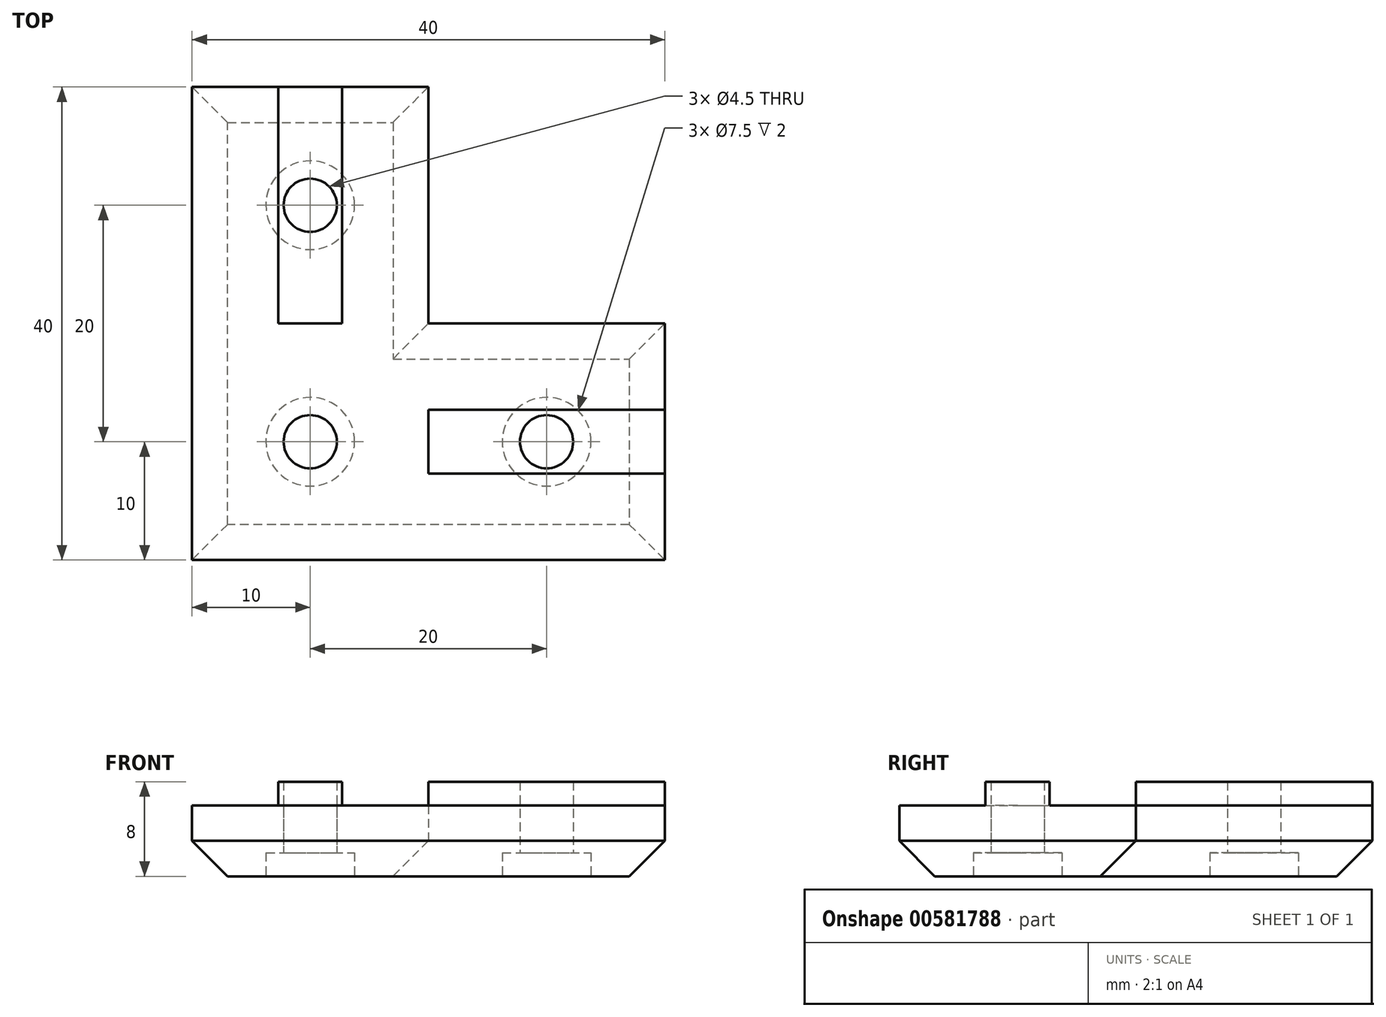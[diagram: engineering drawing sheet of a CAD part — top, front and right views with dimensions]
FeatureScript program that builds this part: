
annotation { "Feature Type Name" : "Feature", "Feature Type Description" : "" }
export const myFeature = defineFeature(function(context is Context, id is Id, definition is map)
    precondition{}
    {
        {
            var Q0;
            Q0=qCreatedBy(makeId("Top.planeOp"),FACE);
            var sketch = newSketch(context, id + "F0", { "sketchPlane" : qUnion([Q0])});
            skLineSegment(sketch, "E0", {"start": v(0, 0) * mm, "end": v(0, 40) * mm});
            skLineSegment(sketch, "E1", {"start": v(0, 40) * mm, "end": v(20, 40) * mm});
            skLineSegment(sketch, "E2", {"start": v(20, 40) * mm, "end": v(20, 20) * mm});
            skLineSegment(sketch, "E3", {"start": v(20, 20) * mm, "end": v(40, 20) * mm});
            skLineSegment(sketch, "E4", {"start": v(40, 20) * mm, "end": v(40, 0) * mm});
            skLineSegment(sketch, "E5", {"start": v(40, 0) * mm, "end": v(0, 0) * mm});
            skSolve(sketch);
        }
        {
            var Q0;
            Q0=qSketchRegion(id+"F0",true);
            extrude(context, id + "F1", {"entities" : qUnion([Q0]), "depth" : 6 * mm});
        }
        {
            var Q0;
            Q0=makeQuery(id+"F1.opExtrude","CAP_FACE",FACE,{"disambiguationData":[OSD([sQuery(id+"F0.wireOp",EDGE,"E0"),sQuery(id+"F0.wireOp",EDGE,"E1"),sQuery(id+"F0.wireOp",EDGE,"E2"),sQuery(id+"F0.wireOp",EDGE,"E3"),sQuery(id+"F0.wireOp",EDGE,"E4"),sQuery(id+"F0.wireOp",EDGE,"E5")])],"isStart":false});
            var sketch = newSketch(context, id + "F2", { "sketchPlane" : qUnion([Q0])});
            skLineSegment(sketch, "E6", {"start": v(7.3, 40) * mm, "end": v(12.71, 40) * mm});
            skLineSegment(sketch, "E7", {"start": v(12.71, 40) * mm, "end": v(12.71, 20) * mm});
            skLineSegment(sketch, "E8", {"start": v(12.71, 20) * mm, "end": v(10, 20) * mm});
            skPoint(sketch, "E8.endSnap0", {"position": v(10, 40) * mm});
            skLineSegment(sketch, "E9", {"start": v(10, 20) * mm, "end": v(7.3, 20) * mm});
            skLineSegment(sketch, "E10", {"start": v(7.3, 20) * mm, "end": v(7.3, 40) * mm});
            skLineSegment(sketch, "E11", {"start": v(40, 12.71) * mm, "end": v(40, 7.3) * mm});
            skLineSegment(sketch, "E12", {"start": v(40, 7.3) * mm, "end": v(20, 7.3) * mm});
            skLineSegment(sketch, "E13", {"start": v(20, 7.3) * mm, "end": v(20, 10) * mm});
            skPoint(sketch, "E13.endSnap0", {"position": v(40, 10) * mm});
            skLineSegment(sketch, "E14", {"start": v(20, 10) * mm, "end": v(20, 12.71) * mm});
            skLineSegment(sketch, "E15", {"start": v(20, 12.71) * mm, "end": v(40, 12.71) * mm});
            skSolve(sketch);
        }
        {
            var Q0;
            Q0=qSketchRegion(id+"F2",true);
            extrude(context, id + "F3", {"entities" : qUnion([Q0]), "operationType" : NewBodyOperationType.ADD, "depth" : 2 * mm});
        }
        {
            var Q0;
            Q0=makeQuery(id+"F1.opExtrude","CAP_FACE",FACE,{"disambiguationData":[OSD([sQuery(id+"F0.wireOp",EDGE,"E0"),sQuery(id+"F0.wireOp",EDGE,"E1"),sQuery(id+"F0.wireOp",EDGE,"E2"),sQuery(id+"F0.wireOp",EDGE,"E3"),sQuery(id+"F0.wireOp",EDGE,"E4"),sQuery(id+"F0.wireOp",EDGE,"E5")])],"isStart":true});
            var sketch = newSketch(context, id + "F4", { "sketchPlane" : qUnion([Q0])});
            skCircle(sketch, "E16", {"center": v(10, -30) * mm, "radius": 2.25 * mm});
            skCircle(sketch, "E17", {"center": v(10, -10) * mm, "radius": 2.25 * mm});
            skCircle(sketch, "E18", {"center": v(30, -10) * mm, "radius": 2.25 * mm});
            skSolve(sketch);
        }
        {
            var Q0;
            Q0=qSketchRegion(id+"F4",true);
            extrude(context, id + "F5", {"entities" : qUnion([Q0]), "operationType" : NewBodyOperationType.REMOVE, "endBound" : BoundingType.THROUGH_ALL, "oppositeDirection" : true, "depth" : 25 * mm});
        }
        {
            var Q0;
            Q0=makeQuery(id+"F1.opExtrude","CAP_FACE",FACE,{"disambiguationData":[OSD([sQuery(id+"F0.wireOp",EDGE,"E0"),sQuery(id+"F0.wireOp",EDGE,"E1"),sQuery(id+"F0.wireOp",EDGE,"E2"),sQuery(id+"F0.wireOp",EDGE,"E3"),sQuery(id+"F0.wireOp",EDGE,"E4"),sQuery(id+"F0.wireOp",EDGE,"E5")])],"isStart":true});
            var sketch = newSketch(context, id + "F6", { "sketchPlane" : qUnion([Q0])});
            skCircle(sketch, "E19", {"center": v(10, -10) * mm, "radius": 3.75 * mm});
            skCircle(sketch, "E20", {"center": v(30, -10) * mm, "radius": 3.75 * mm});
            skCircle(sketch, "E21", {"center": v(10, -30) * mm, "radius": 3.75 * mm});
            skSolve(sketch);
        }
        {
            var Q0;
            Q0=qSketchRegion(id+"F6",true);
            extrude(context, id + "F7", {"entities" : qUnion([Q0]), "operationType" : NewBodyOperationType.REMOVE, "oppositeDirection" : true, "depth" : 2 * mm});
        }
        {
            var Q0;
            Q0=makeQuery(id+"F1.opExtrude","CAP_EDGE",EDGE,{"disambiguationData":[OSD([sQuery(id+"F0.wireOp",EDGE,"E5")])],"isStart":true});
            var Q1;
            Q1=makeQuery(id+"F1.opExtrude","CAP_EDGE",EDGE,{"disambiguationData":[OSD([sQuery(id+"F0.wireOp",EDGE,"E0")])],"isStart":true});
            var Q2;
            Q2=makeQuery(id+"F1.opExtrude","CAP_EDGE",EDGE,{"disambiguationData":[OSD([sQuery(id+"F0.wireOp",EDGE,"E2")])],"isStart":true});
            var Q3;
            Q3=makeQuery(id+"F1.opExtrude","CAP_EDGE",EDGE,{"disambiguationData":[OSD([sQuery(id+"F0.wireOp",EDGE,"E3")])],"isStart":true});
            var Q4;
            Q4=makeQuery(id+"F1.opExtrude","CAP_EDGE",EDGE,{"disambiguationData":[OSD([sQuery(id+"F0.wireOp",EDGE,"E4")])],"isStart":true});
            var Q5;
            Q5=makeQuery(id+"F1.opExtrude","CAP_EDGE",EDGE,{"disambiguationData":[OSD([sQuery(id+"F0.wireOp",EDGE,"E1")])],"isStart":true});
            chamfer(context, id + "F8", {"entities" : qUnion([Q0, Q1, Q2, Q3, Q4, Q5]), "width" : 3 * mm, "tangentPropagation" : true});
        }
    });
